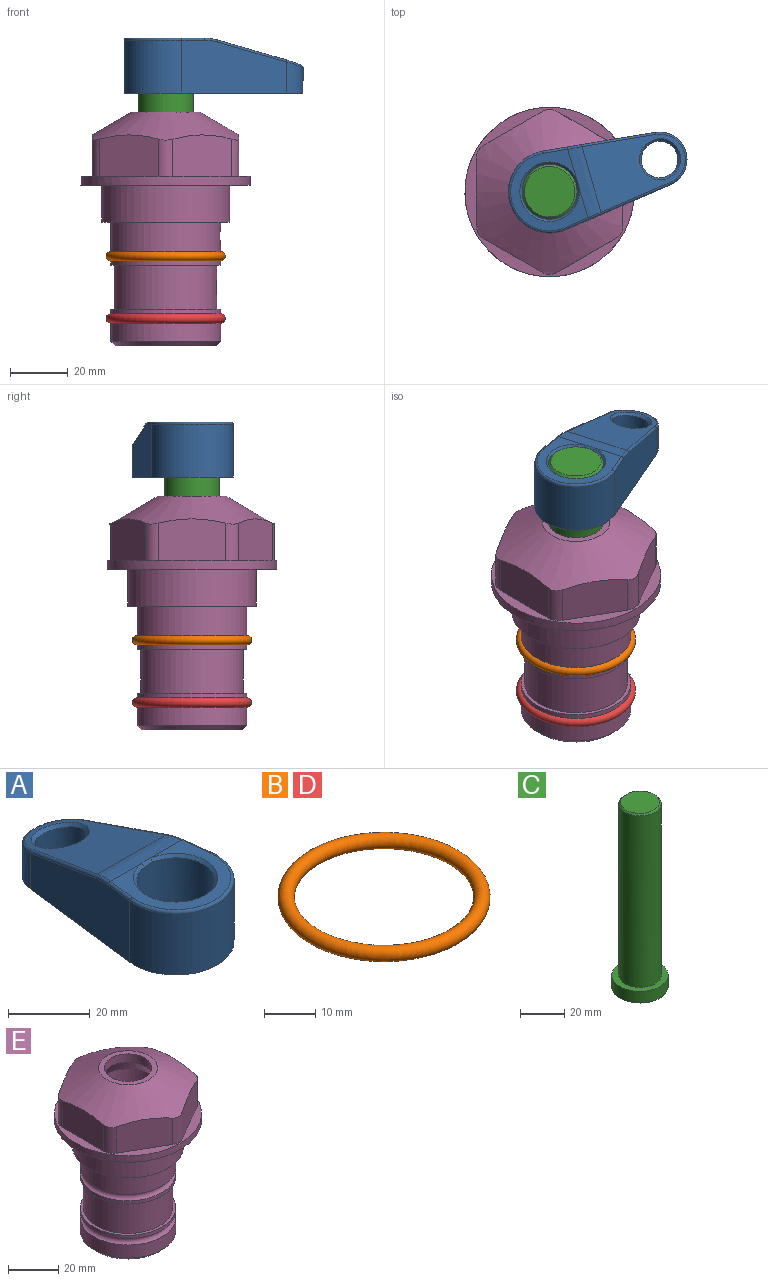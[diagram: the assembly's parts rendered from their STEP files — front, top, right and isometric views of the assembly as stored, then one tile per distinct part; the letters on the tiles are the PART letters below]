
ASSEMBLY  parts=5 mates=4
PART A: 31 faces, bbox 31.7x65.5x19.8 mm
  f0: plane 39.12x18.26mm, normal (0.99,0.12,0), area 612.2mm2, adj f1,f4,f7,f11,f13,f15
  f1: cylinder r=9.53mm len=18.91mm, axis (0,0,-1), area 296.1mm2, adj f0,f2,f7,f17
  f2: plane 39.12x18.26mm, normal (-0.99,0.12,0), area 612.2mm2, adj f1,f4,f7,f12,f14,f16
  f3: cylinder r=6.35mm len=12.7mm, axis (0,0,-1), area 362.4mm2, adj f7,f18
  f4: cylinder r=14.29mm len=28.58mm, axis (0,0,-1), area 882.2mm2, adj f0,f2,f7,f10
  f5: cylinder r=9.53mm len=19.05mm, axis (0,0,-1), area 1092.6mm2, adj f7,f19,f20
  f6: plane 26.99x23.69mm, normal (0,0,1), area 216.2mm2, adj f9,f10,f11,f12,f19
  f7: plane 63.5x28.58mm, normal (0,0,-1), area 661.8mm2, adj f0,f1,f2,f3,f4,f5,f22,f23
  f8: plane 33.52x23.6mm, normal (0,0.26,0.97), area 486mm2, adj f9,f15,f16,f17,f18
  f9: cylinder r=19.05mm len=24.72mm, axis (1,0,0), area 120.4mm2, adj f6,f8,f13,f14,f20
  f10: torus R=13.49mm, axis (0,0,1), area 59mm2, adj f4,f6,f11,f12
  f11: cylinder r=0.79mm len=8.67mm, axis (0.12,-0.99,0), area 10.8mm2, adj f0,f6,f10,f13
  f12: cylinder r=0.79mm len=8.67mm, axis (0.12,0.99,0), area 10.8mm2, adj f2,f6,f10,f14
  f13: bspline ~4.95x1.42mm, area 6.1mm2, adj f0,f9,f11,f15
  f14: bspline ~4.95x1.42mm, area 6.1mm2, adj f2,f9,f12,f16
  f15: cylinder r=0.79mm len=25.95mm, axis (0.12,-0.96,0.26), area 32.9mm2, adj f0,f8,f13,f17
  f16: cylinder r=0.79mm len=25.95mm, axis (0.12,0.96,-0.26), area 32.9mm2, adj f2,f8,f14,f17
  f17: bspline ~18.91x8.38mm, area 30mm2, adj f1,f8,f15,f16
  f18: bspline ~14.29x14.29mm, area 48.3mm2, adj f3,f8
  f19: cone r=9.53mm half-angle=45deg, axis (0,0,1), area 66.5mm2, adj f5,f6,f20
  f20: bspline ~3.22x0.96mm, area 3.5mm2, adj f5,f9,f19
  f21: plane 2.75x2.72mm, normal (0,0,-1), area 2.9mm2, adj f23,f25,f28
  f22: plane 23.05x15.88mm, normal (-0.99,-0.12,0), area 323.6mm2, adj f7,f25,f26,f27,f28,f29
  f23: plane 23.05x15.88mm, normal (0.99,-0.12,0), area 323.6mm2, adj f7,f21,f25,f27,f28,f30
  f24: cylinder r=9.53mm len=10.69mm, axis (0,0,-1), area 114.7mm2, adj f7,f27,f29,f30
  f25: cylinder r=12.7mm len=20.59mm, axis (0,0,-1), area 381.1mm2, adj f7,f21,f22,f23,f26,f28
  f26: plane 2.75x2.72mm, normal (0,0,-1), area 2.9mm2, adj f22,f25,f28
  f27: plane 19.72x18.37mm, normal (0,-0.26,-0.97), area 291.8mm2, adj f22,f23,f24,f28,f29,f30
  f28: cylinder r=15.88mm len=19.92mm, axis (1,0,0), area 54.8mm2, adj f21,f22,f23,f25,f26,f27
  f29: cylinder r=1.59mm len=11mm, axis (0,0,-1), area 34.7mm2, adj f7,f22,f24,f27
  f30: cylinder r=1.59mm len=11mm, axis (0,0,-1), area 34.7mm2, adj f7,f23,f24,f27
PART B: 1 faces, bbox 44.7x44.7x3.2 mm
  f0: torus R=19.05mm, axis (0,0,1), area 1193.9mm2
PART C: 6 faces, bbox 25.4x25.4x101.6 mm
  f0: plane 17.46x17.46mm, normal (0,0,1), area 239.5mm2, adj f5
  f1: plane 25.4x25.4mm, normal (0,0,-1), area 506.7mm2, adj f2
  f2: cylinder r=12.7mm len=25.4mm, axis (0,0,1), area 506.7mm2, adj f1,f3
  f3: plane 25.4x25.4mm, normal (0,0,1), area 221.7mm2, adj f2,f4
  f4: cylinder r=9.53mm len=94.46mm, axis (0,0,1), area 5653mm2, adj f3,f5
  f5: cone r=8.73mm half-angle=45deg, axis (0,0,-1), area 64.4mm2, adj f0,f4
PART D: same geometry as B
PART E: 36 faces, bbox 58.7x58.7x81 mm
  f0: cylinder r=17.78mm len=35.56mm, axis (0,0,1), area 1670.8mm2, adj f23,f24,f31
  f1: cylinder r=19.05mm len=38.1mm, axis (0,0,1), area 1191.9mm2, adj f26,f27,f30
  f2: plane 58.66x58.66mm, normal (0,0,-1), area 1150.6mm2, adj f3,f28
  f3: cylinder r=29.33mm len=58.66mm, axis (0,0,-1), area 585.1mm2, adj f2,f4
  f4: plane 58.66x58.66mm, normal (0,0,1), area 475.9mm2, adj f3,f5,f6,f7,f8,f9,f10,f11
  f5: plane 20.32x14.34mm, normal (-0.5,0.87,0), area 324.4mm2, adj f4,f15,f16,f17
  f6: plane 20.32x14.34mm, normal (0.5,0.87,0), area 324.4mm2, adj f4,f14,f15,f17
  f7: plane 23.48x14.34mm, normal (1,0,0), area 324.4mm2, adj f4,f13,f14,f17
  f8: plane 20.32x14.34mm, normal (0.5,-0.87,0), area 324.4mm2, adj f4,f12,f13,f17
  f9: plane 20.32x14.34mm, normal (-0.5,-0.87,0), area 324.4mm2, adj f4,f11,f12,f17
  f10: plane 23.48x14.34mm, normal (-1,0,0), area 324.4mm2, adj f4,f11,f16,f17
  f11: cylinder r=5.08mm len=12.85mm, axis (0,0,-1), area 67.2mm2, adj f4,f9,f10,f17
  f12: cylinder r=5.08mm len=12.85mm, axis (0,0,-1), area 67.2mm2, adj f4,f8,f9,f17
  f13: cylinder r=5.08mm len=12.85mm, axis (0,0,-1), area 67.2mm2, adj f4,f7,f8,f17
  f14: cylinder r=5.08mm len=12.85mm, axis (0,0,-1), area 67.2mm2, adj f4,f6,f7,f17
  f15: cylinder r=5.08mm len=12.85mm, axis (0,0,-1), area 67.2mm2, adj f4,f5,f6,f17
  f16: cylinder r=5.08mm len=12.85mm, axis (0,0,-1), area 67.2mm2, adj f4,f5,f10,f17
  f17: cone r=11.73mm half-angle=60deg, axis (0,0,-1), area 2071.8mm2, adj f5,f6,f7,f8,f9,f10,f11,f12
  f18: plane 23.46x23.46mm, normal (0,0,1), area 147.4mm2, adj f17,f35
  f19: plane 34.93x34.93mm, normal (0,0,-1), area 958mm2, adj f29
  f20: cylinder r=19.05mm len=38.1mm, axis (0,0,1), area 760.1mm2, adj f21,f29
  f21: torus R=19.05mm, axis (0,0,1), area 565.3mm2, adj f20,f22
  f22: cylinder r=19.05mm len=38.1mm, axis (0,0,1), area 190mm2, adj f21,f23
  f23: plane 38.1x38.1mm, normal (0,0,1), area 146.9mm2, adj f0,f22
  f24: plane 38.1x38.1mm, normal (0,0,-1), area 146.9mm2, adj f0,f25
  f25: cylinder r=19.05mm len=38.1mm, axis (0,0,1), area 190mm2, adj f24,f26
  f26: torus R=19.05mm, axis (0,0,1), area 565.3mm2, adj f1,f25
  f27: plane 44.45x44.45mm, normal (0,0,-1), area 411.7mm2, adj f1,f28
  f28: cylinder r=22.23mm len=44.45mm, axis (0,0,1), area 1773.5mm2, adj f2,f27
  f29: cone r=19.05mm half-angle=45deg, axis (0,0,1), area 257.5mm2, adj f19,f20
  f30: cylinder r=3.17mm len=6.75mm, axis (-1,0,0), area 128mm2, adj f1,f33
  f31: cylinder r=3.17mm len=6.35mm, axis (-1,0,0), area 102.5mm2, adj f0,f33
  f32: plane 25.4x25.4mm, normal (0,0,1), area 506.7mm2, adj f33
  f33: cylinder r=12.7mm len=66.42mm, axis (0,0,-1), area 5236.2mm2, adj f30,f31,f32,f34
  f34: cone r=9.53mm half-angle=30deg, axis (0,0,-1), area 443.4mm2, adj f33,f35
  f35: cylinder r=9.53mm len=19.05mm, axis (0,0,-1), area 240.9mm2, adj f18,f34
PLACE A rot(axis=(0,0,-1),73.6deg) t=(0,0,-12.45)mm
PLACE B at identity
PLACE C rot(axis=(0,0,-1),73.6deg) t=(0,0,-12.45)mm
PLACE D t=(0,0,-21.59)mm
PLACE E at identity fixed
MATE fastened A.f4 <-> C.f2  axis (0,0,1) through (0,0,51.05)mm
MATE cylindrical C.f2 <-> E.f0  axis (0,0,-1) through (0,0,-50.55)mm
MATE fastened D.f0 <-> E.f0  axis (0,0,1) through (0,0,-46.1)mm
MATE fastened B.f0 <-> E.f0  axis (0,0,1) through (0,0,-24.51)mm
